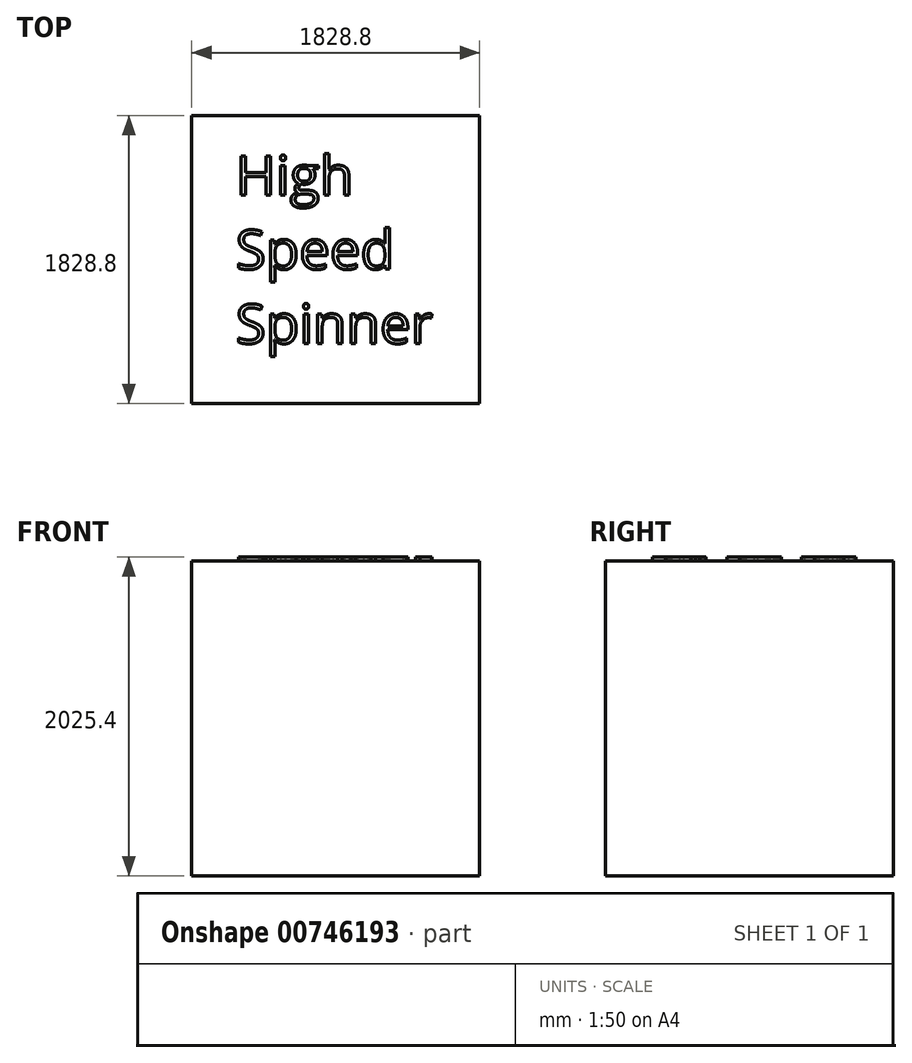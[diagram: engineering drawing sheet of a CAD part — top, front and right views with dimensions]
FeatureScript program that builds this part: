
annotation { "Feature Type Name" : "Feature", "Feature Type Description" : "" }
export const myFeature = defineFeature(function(context is Context, id is Id, definition is map)
    precondition{}
    {
        {
            var Q0;
            Q0=qCreatedBy(makeId("Top.planeOp"),FACE);
            var sketch = newSketch(context, id + "F0", { "sketchPlane" : qUnion([Q0])});
            skLineSegment(sketch, "E0.bottom", {"start": v(914.4, -914.4) * mm, "end": v(-914.4, -914.4) * mm});
            skLineSegment(sketch, "E0.top", {"start": v(914.4, 914.4) * mm, "end": v(-914.4, 914.4) * mm});
            skLineSegment(sketch, "E0.left", {"start": v(914.4, -914.4) * mm, "end": v(914.4, 914.4) * mm});
            skLineSegment(sketch, "E0.right", {"start": v(-914.4, -914.4) * mm, "end": v(-914.4, 914.4) * mm});
            skPoint(sketch, "E0.middle", {"position": v(0, 0) * mm});
            skSolve(sketch);
        }
        {
            var Q0;
            Q0 = qSketchRegion(id + "F0", true);
            extrude(context, id + "F1", {"entities" : qUnion([Q0]), "depth" : 2000 * mm, "offsetDistance" : 25.4 * mm});
        }
        {
            var Q0;
            Q0=makeQuery(id+"F1.opExtrude","CAP_FACE",FACE,{"disambiguationData":[OSD([sQuery(id+"F0.wireOp",EDGE,"E0.bottom"),sQuery(id+"F0.wireOp",EDGE,"E0.top"),sQuery(id+"F0.wireOp",EDGE,"E0.left"),sQuery(id+"F0.wireOp",EDGE,"E0.right")])],"isStart":false});
            var sketch = newSketch(context, id + "F2", { "sketchPlane" : qUnion([Q0])});
            skText(sketch, "E1", { "text": "High\nSpeed\nSpinner", "fontName": "OpenSans-Regular.ttf"});
            const initialGuessF2  = {"E1": [-0.635, 0.41071, 1, 0, 0.24969]};
            skSetInitialGuess(sketch, initialGuessF2);
            skSolve(sketch);
        }
        {
            var Q0;
            Q0 = qSketchRegion(id + "F2", true);
            extrude(context, id + "F3", {"entities" : qUnion([Q0]), "operationType" : NewBodyOperationType.ADD, "depth" : 25.4 * mm, "offsetDistance" : 25.4 * mm});
        }
    });
